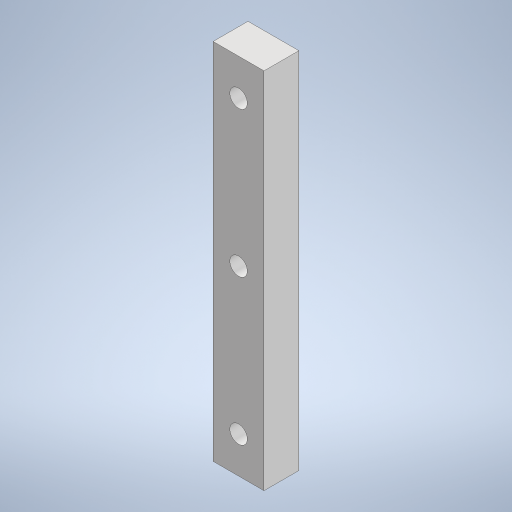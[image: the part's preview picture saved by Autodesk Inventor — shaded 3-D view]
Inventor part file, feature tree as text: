
AUTODESK INVENTOR PART (.ipt)
format: ipt  version: 2024.1 (Build 281209000, 209)  size: 239,616 bytes
history: native  units: in
note: dims shown in document units (in); Inventor stores cm internally (conversion verified against a paired STEP export)
features: extrude x2, sketch x2
ambient origin geometry x8: Origin, YZ Plane, XZ Plane, XY Plane, X Axis, Y Axis, Z Axis, Center Point
bodies: Solid1 (feature_tree)
feature tree (4):
  extrude  "Extrusion1"  Depth=0.2756in
  extrude  "Extrusion2"  Depth=0.3937in
  sketch  "Sketch1"  dims[d0=0.189in d1=0.2756in]
  sketch  "Sketch2"  dims[d2=1.9685in d3=0.0in d4=0.0945in d5=0.1969in d6=0.1378in d7=1.1811in d9=0.7874in d10=0.3937in d12=0.3937in d14=0.0in d15=0.0in]
